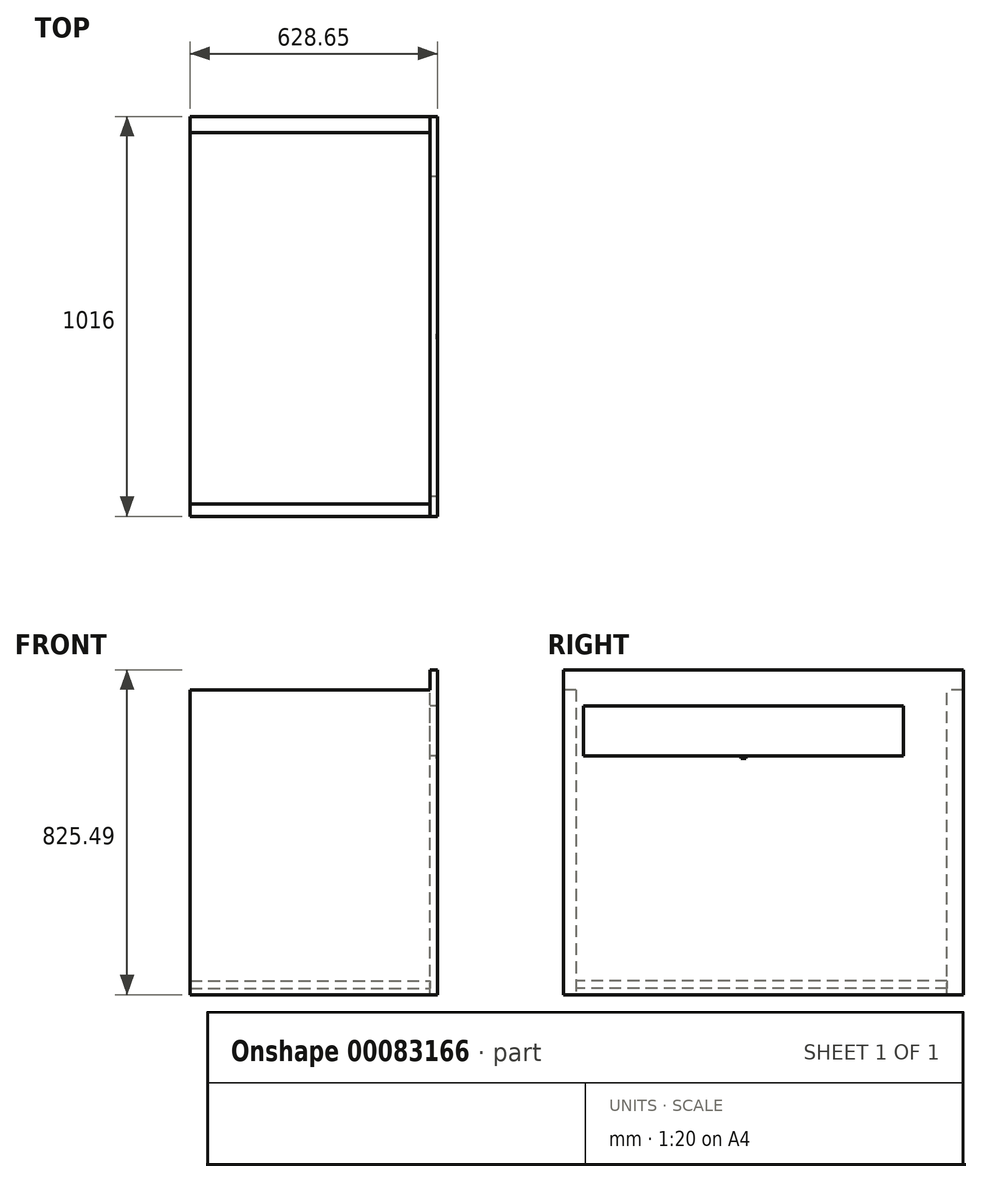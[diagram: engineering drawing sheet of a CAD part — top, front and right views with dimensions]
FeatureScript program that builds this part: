
annotation { "Feature Type Name" : "Feature", "Feature Type Description" : "" }
export const myFeature = defineFeature(function(context is Context, id is Id, definition is map)
    precondition{}
    {
        {
            var Q0;
            Q0=qCreatedBy(makeId("Right.planeOp"),FACE);
            var sketch = newSketch(context, id + "F0", { "sketchPlane" : qUnion([Q0])});
            skLineSegment(sketch, "E0.bottom", {"start": v(457.2, 104.77) * mm, "end": v(-457.2, 104.77) * mm});
            skLineSegment(sketch, "E0.top", {"start": v(457.2, -104.77) * mm, "end": v(-457.2, -104.77) * mm});
            skLineSegment(sketch, "E0.left", {"start": v(457.2, 104.78) * mm, "end": v(457.2, -104.78) * mm});
            skLineSegment(sketch, "E0.right", {"start": v(-457.2, 104.78) * mm, "end": v(-457.2, -104.78) * mm});
            skPoint(sketch, "E0.middle", {"position": v(0, 0) * mm});
            skLineSegment(sketch, "E1.bottom", {"start": v(-406.4, -63.5) * mm, "end": v(406.4, -63.5) * mm});
            skLineSegment(sketch, "E1.top", {"start": v(-406.4, 63.5) * mm, "end": v(406.4, 63.5) * mm});
            skLineSegment(sketch, "E1.left", {"start": v(-406.4, -63.5) * mm, "end": v(-406.4, 63.5) * mm});
            skLineSegment(sketch, "E1.right", {"start": v(406.4, -63.5) * mm, "end": v(406.4, 63.5) * mm});
            skSolve(sketch);
        }
        {
            var Q0;
            Q0=makeQuery(id+"F0.imprint","IMPRINT",FACE,{"disambiguationData":[TD([[makeQuery(id+"F0.imprint","IMPRINT",EDGE,{"derivedFrom":sQuery(id+"F0.wireOp",EDGE,"E0.bottom")}),1.0]])]});
            extrude(context, id + "F1", {"entities" : qUnion([Q0]), "depth" : 19.05 * mm});
        }
        {
            var Q0;
            Q0=makeQuery(id+"F1.opExtrude","CAP_FACE",FACE,{"disambiguationData":[OSD([sQuery(id+"F0.wireOp",EDGE,"E0.bottom"),sQuery(id+"F0.wireOp",EDGE,"E0.top"),sQuery(id+"F0.wireOp",EDGE,"E0.left"),sQuery(id+"F0.wireOp",EDGE,"E0.right"),sQuery(id+"F0.wireOp",EDGE,"E1.bottom"),sQuery(id+"F0.wireOp",EDGE,"E1.top"),sQuery(id+"F0.wireOp",EDGE,"E1.left"),sQuery(id+"F0.wireOp",EDGE,"E1.right")])],"isStart":false});
            var sketch = newSketch(context, id + "F2", { "sketchPlane" : qUnion([Q0])});
            skLineSegment(sketch, "E2.bottom", {"start": v(-6.35, -69.85) * mm, "end": v(6.35, -69.85) * mm});
            skLineSegment(sketch, "E2.top", {"start": v(-6.35, -57.15) * mm, "end": v(6.35, -57.15) * mm});
            skLineSegment(sketch, "E2.left", {"start": v(-6.35, -69.85) * mm, "end": v(-6.35, -57.15) * mm});
            skLineSegment(sketch, "E2.right", {"start": v(6.35, -69.85) * mm, "end": v(6.35, -57.15) * mm});
            skPoint(sketch, "E2.middle", {"position": v(0, -63.5) * mm});
            skSolve(sketch);
        }
        {
            var Q0;
            {var subQ0=sQuery(id+"F2.wireOp",EDGE,"E2.bottom");Q0=makeQuery(id+"F2.imprint","IMPRINT",FACE,{"disambiguationData":[TD([[makeQuery(id+"F2.imprint","IMPRINT",EDGE,{"derivedFrom":subQ0}),1.0]])]});}
            extrude(context, id + "F3", {"entities" : qUnion([Q0]), "operationType" : NewBodyOperationType.REMOVE, "oppositeDirection" : true, "depth" : 2.54 * mm});
        }
        {
            var Q0;
            Q0=makeQuery(id+"F1.opExtrude","SWEPT_FACE",FACE,{"disambiguationData":[OSD([sQuery(id+"F0.wireOp",EDGE,"E0.top")])]});
            var sketch = newSketch(context, id + "F4", { "sketchPlane" : qUnion([Q0])});
            skLineSegment(sketch, "E3.0", {"start": v(19.05, -457.2) * mm, "end": v(19.05, 457.2) * mm});
            skLineSegment(sketch, "E4.0", {"start": v(19.05, 457.2) * mm, "end": v(0, 457.2) * mm});
            skLineSegment(sketch, "E5.0", {"start": v(0, -457.2) * mm, "end": v(0, 457.2) * mm});
            skLineSegment(sketch, "E6.0", {"start": v(19.05, -457.2) * mm, "end": v(0, -457.2) * mm});
            skSolve(sketch);
        }
        {
            var Q0;
            Q0 = qSketchRegion(id + "F4", true);
            extrude(context, id + "F5", {"entities" : qUnion([Q0]), "operationType" : NewBodyOperationType.ADD, "depth" : 565.15 * mm});
        }
        {
            var Q0;
            Q0=makeQuery(id+"F5.boolean.opBoolean","MERGE",FACE,{"derivedFrom":[makeQuery(id+"F1.opExtrude","SWEPT_FACE",FACE,{"disambiguationData":[OSD([sQuery(id+"F0.wireOp",EDGE,"E0.left")])]}),makeQuery(id+"F5.opExtrude","SWEPT_FACE",FACE,{"disambiguationData":[OSD([sQuery(id+"F4.wireOp",EDGE,"E6.0")])]})]});
            var sketch = newSketch(context, id + "F6", { "sketchPlane" : qUnion([Q0])});
            skLineSegment(sketch, "E7.0", {"start": v(0, 104.77) * mm, "end": v(0, -669.93) * mm});
            skLineSegment(sketch, "E8.0", {"start": v(-19.05, 104.77) * mm, "end": v(0, 104.77) * mm});
            skLineSegment(sketch, "E9.0", {"start": v(-19.05, 104.77) * mm, "end": v(-19.05, -669.93) * mm});
            skLineSegment(sketch, "E10.0", {"start": v(-19.05, -669.93) * mm, "end": v(0, -669.93) * mm});
            skSolve(sketch);
        }
        {
            var Q0;
            Q0 = qSketchRegion(id + "F6", true);
            extrude(context, id + "F7", {"entities" : qUnion([Q0]), "operationType" : NewBodyOperationType.ADD, "depth" : 101.6 * mm});
        }
        {
            var Q0;
            Q0=makeQuery(id+"F7.boolean.opBoolean","MERGE",FACE,{"derivedFrom":[makeQuery(id+"F5.boolean.opBoolean","MERGE",FACE,{"derivedFrom":[makeQuery(id+"F1.opExtrude","CAP_FACE",FACE,{"disambiguationData":[OSD([sQuery(id+"F0.wireOp",EDGE,"E0.bottom"),sQuery(id+"F0.wireOp",EDGE,"E0.top"),sQuery(id+"F0.wireOp",EDGE,"E0.left"),sQuery(id+"F0.wireOp",EDGE,"E0.right"),sQuery(id+"F0.wireOp",EDGE,"E1.bottom"),sQuery(id+"F0.wireOp",EDGE,"E1.top"),sQuery(id+"F0.wireOp",EDGE,"E1.left"),sQuery(id+"F0.wireOp",EDGE,"E1.right")])],"isStart":false}),makeQuery(id+"F5.opExtrude","SWEPT_FACE",FACE,{"disambiguationData":[OSD([sQuery(id+"F4.wireOp",EDGE,"E3.0")])]})]}),makeQuery(id+"F7.opExtrude","SWEPT_FACE",FACE,{"disambiguationData":[OSD([sQuery(id+"F6.wireOp",EDGE,"E9.0")])]})]});
            var sketch = newSketch(context, id + "F8", { "sketchPlane" : qUnion([Q0])});
            skLineSegment(sketch, "E11.bottom", {"start": v(-406.4, -114.3) * mm, "end": v(406.4, -114.3) * mm});
            skLineSegment(sketch, "E11.top", {"start": v(-406.4, -635) * mm, "end": v(406.4, -635) * mm});
            skLineSegment(sketch, "E11.left", {"start": v(-406.4, -114.3) * mm, "end": v(-406.4, -635) * mm});
            skLineSegment(sketch, "E11.right", {"start": v(406.4, -114.3) * mm, "end": v(406.4, -635) * mm});
            skSolve(sketch);
        }
        {
            var Q0;
            Q0=makeQuery(id+"F7.boolean.opBoolean","MERGE",FACE,{"derivedFrom":[makeQuery(id+"F5.boolean.opBoolean","MERGE",FACE,{"derivedFrom":[makeQuery(id+"F1.opExtrude","CAP_FACE",FACE,{"disambiguationData":[OSD([sQuery(id+"F0.wireOp",EDGE,"E0.bottom"),sQuery(id+"F0.wireOp",EDGE,"E0.top"),sQuery(id+"F0.wireOp",EDGE,"E0.left"),sQuery(id+"F0.wireOp",EDGE,"E0.right"),sQuery(id+"F0.wireOp",EDGE,"E1.bottom"),sQuery(id+"F0.wireOp",EDGE,"E1.top"),sQuery(id+"F0.wireOp",EDGE,"E1.left"),sQuery(id+"F0.wireOp",EDGE,"E1.right")])],"isStart":true}),makeQuery(id+"F5.opExtrude","SWEPT_FACE",FACE,{"disambiguationData":[OSD([sQuery(id+"F4.wireOp",EDGE,"E5.0")])]})]}),makeQuery(id+"F7.opExtrude","SWEPT_FACE",FACE,{"disambiguationData":[OSD([sQuery(id+"F6.wireOp",EDGE,"E7.0")])]})]});
            var sketch = newSketch(context, id + "F9", { "sketchPlane" : qUnion([Q0])});
            skLineSegment(sketch, "E12.0", {"start": v(457.2, 104.78) * mm, "end": v(457.2, -669.93) * mm});
            skLineSegment(sketch, "E13.0", {"start": v(-558.8, 104.77) * mm, "end": v(457.2, 104.77) * mm});
            skLineSegment(sketch, "E14.0", {"start": v(-558.8, -669.92) * mm, "end": v(457.2, -669.92) * mm});
            skLineSegment(sketch, "E15", {"start": v(425.45, 104.78) * mm, "end": v(425.45, -669.92) * mm});
            skSolve(sketch);
        }
        {
            var Q0;
            Q0 = qSketchRegion(id + "F9", true);
            extrude(context, id + "F10", {"entities" : qUnion([Q0]), "depth" : 609.6 * mm});
        }
        {
            var Q0;
            Q0=makeQuery(id+"F7.boolean.opBoolean","MERGE",FACE,{"derivedFrom":[makeQuery(id+"F5.boolean.opBoolean","MERGE",FACE,{"derivedFrom":[makeQuery(id+"F1.opExtrude","CAP_FACE",FACE,{"disambiguationData":[OSD([sQuery(id+"F0.wireOp",EDGE,"E0.bottom"),sQuery(id+"F0.wireOp",EDGE,"E0.top"),sQuery(id+"F0.wireOp",EDGE,"E0.left"),sQuery(id+"F0.wireOp",EDGE,"E0.right"),sQuery(id+"F0.wireOp",EDGE,"E1.bottom"),sQuery(id+"F0.wireOp",EDGE,"E1.top"),sQuery(id+"F0.wireOp",EDGE,"E1.left"),sQuery(id+"F0.wireOp",EDGE,"E1.right")])],"isStart":true}),makeQuery(id+"F5.opExtrude","SWEPT_FACE",FACE,{"disambiguationData":[OSD([sQuery(id+"F4.wireOp",EDGE,"E5.0")])]})]}),makeQuery(id+"F7.opExtrude","SWEPT_FACE",FACE,{"disambiguationData":[OSD([sQuery(id+"F6.wireOp",EDGE,"E7.0")])]})]});
            var sketch = newSketch(context, id + "F11", { "sketchPlane" : qUnion([Q0])});
            skLineSegment(sketch, "E16", {"start": v(-517.53, -669.92) * mm, "end": v(-517.53, 104.78) * mm});
            skLineSegment(sketch, "E17.0", {"start": v(-558.8, 104.77) * mm, "end": v(457.2, 104.77) * mm});
            skLineSegment(sketch, "E18.0", {"start": v(-558.8, 104.78) * mm, "end": v(-558.8, -669.93) * mm});
            skLineSegment(sketch, "E19.0", {"start": v(-558.8, -669.92) * mm, "end": v(457.2, -669.92) * mm});
            skSolve(sketch);
        }
        {
            var Q0;
            {var subQ0=sQuery(id+"F11.wireOp",EDGE,"E16");Q0=makeQuery(id+"F11.imprint","IMPRINT",FACE,{"disambiguationData":[TD([[makeQuery(id+"F11.imprint","IMPRINT",EDGE,{"derivedFrom":subQ0}),1.0]])]});}
            extrude(context, id + "F12", {"entities" : qUnion([Q0]), "depth" : 609.6 * mm});
        }
        {
            var Q0;
            Q0=makeQuery(id+"F7.boolean.opBoolean","MERGE",FACE,{"derivedFrom":[makeQuery(id+"F5.boolean.opBoolean","MERGE",FACE,{"derivedFrom":[makeQuery(id+"F1.opExtrude","CAP_FACE",FACE,{"disambiguationData":[OSD([sQuery(id+"F0.wireOp",EDGE,"E0.bottom"),sQuery(id+"F0.wireOp",EDGE,"E0.top"),sQuery(id+"F0.wireOp",EDGE,"E0.left"),sQuery(id+"F0.wireOp",EDGE,"E0.right"),sQuery(id+"F0.wireOp",EDGE,"E1.bottom"),sQuery(id+"F0.wireOp",EDGE,"E1.top"),sQuery(id+"F0.wireOp",EDGE,"E1.left"),sQuery(id+"F0.wireOp",EDGE,"E1.right")])],"isStart":true}),makeQuery(id+"F5.opExtrude","SWEPT_FACE",FACE,{"disambiguationData":[OSD([sQuery(id+"F4.wireOp",EDGE,"E5.0")])]})]}),makeQuery(id+"F7.opExtrude","SWEPT_FACE",FACE,{"disambiguationData":[OSD([sQuery(id+"F6.wireOp",EDGE,"E7.0")])]})]});
            var sketch = newSketch(context, id + "F13", { "sketchPlane" : qUnion([Q0])});
            skLineSegment(sketch, "E20.bottom", {"start": v(-517.53, -635) * mm, "end": v(425.45, -635) * mm});
            skLineSegment(sketch, "E20.top", {"start": v(-517.53, -654.05) * mm, "end": v(425.45, -654.05) * mm});
            skLineSegment(sketch, "E20.left", {"start": v(-517.53, -635) * mm, "end": v(-517.53, -654.05) * mm});
            skLineSegment(sketch, "E20.right", {"start": v(425.45, -635) * mm, "end": v(425.45, -654.05) * mm});
            skSolve(sketch);
        }
        {
            var Q0;
            Q0=makeQuery(id+"F13.imprint","IMPRINT",FACE,{"disambiguationData":[TD([[makeQuery(id+"F13.imprint","IMPRINT",EDGE,{"derivedFrom":sQuery(id+"F13.wireOp",EDGE,"E20.top")}),1.0]])]});
            extrude(context, id + "F14", {"entities" : qUnion([Q0]), "depth" : 609.6 * mm});
        }
        {
            var Q0;
            Q0=makeQuery(id+"F7.boolean.opBoolean","MERGE",FACE,{"derivedFrom":[makeQuery(id+"F1.opExtrude","SWEPT_FACE",FACE,{"disambiguationData":[OSD([sQuery(id+"F0.wireOp",EDGE,"E0.bottom")])]}),makeQuery(id+"F7.opExtrude","SWEPT_FACE",FACE,{"disambiguationData":[OSD([sQuery(id+"F6.wireOp",EDGE,"E8.0")])]})]});
            var sketch = newSketch(context, id + "F15", { "sketchPlane" : qUnion([Q0])});
            skLineSegment(sketch, "E21.0", {"start": v(0, 558.8) * mm, "end": v(0, -457.2) * mm});
            skLineSegment(sketch, "E22.0", {"start": v(19.05, -457.2) * mm, "end": v(0, -457.2) * mm});
            skLineSegment(sketch, "E23.0", {"start": v(19.05, 558.8) * mm, "end": v(19.05, -457.2) * mm});
            skLineSegment(sketch, "E24.0", {"start": v(19.05, 558.8) * mm, "end": v(0, 558.8) * mm});
            skSolve(sketch);
        }
        {
            var Q0;
            Q0 = qSketchRegion(id + "F15", true);
            extrude(context, id + "F16", {"entities" : qUnion([Q0]), "operationType" : NewBodyOperationType.ADD, "depth" : 50.8 * mm});
        }
    });
